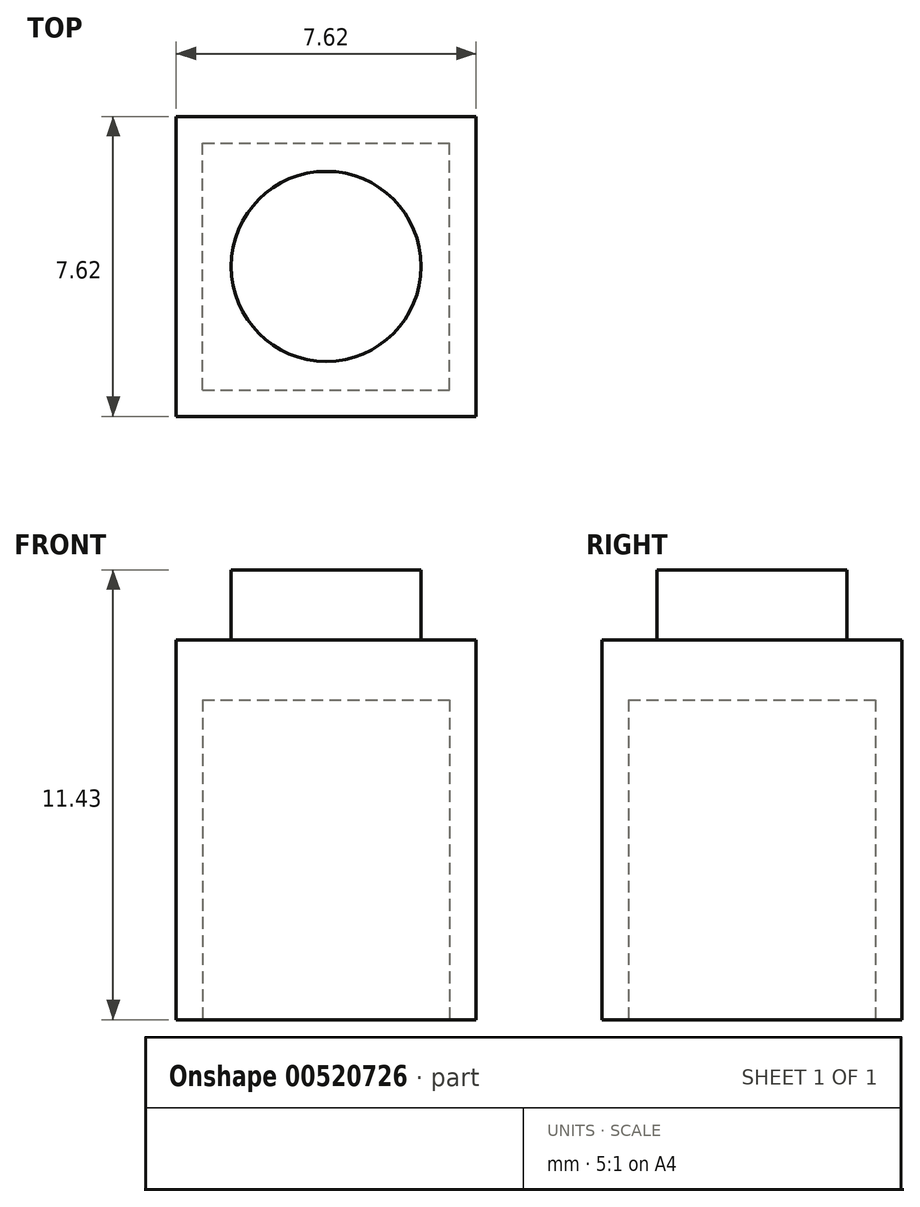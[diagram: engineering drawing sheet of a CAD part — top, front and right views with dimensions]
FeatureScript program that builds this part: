
annotation { "Feature Type Name" : "Feature", "Feature Type Description" : "" }
export const myFeature = defineFeature(function(context is Context, id is Id, definition is map)
    precondition{}
    {
        {
            var Q0;
            Q0=qCreatedBy(makeId("Top.planeOp"),FACE);
            var sketch = newSketch(context, id + "F0", { "sketchPlane" : qUnion([Q0])});
            skLineSegment(sketch, "E0.bottom", {"start": v(-3.8, 3.8) * mm, "end": v(3.81, 3.8) * mm});
            skLineSegment(sketch, "E0.top", {"start": v(-3.81, -3.81) * mm, "end": v(3.8, -3.81) * mm});
            skLineSegment(sketch, "E0.left", {"start": v(-3.8, 3.81) * mm, "end": v(-3.81, -3.81) * mm});
            skLineSegment(sketch, "E0.right", {"start": v(3.81, 3.8) * mm, "end": v(3.8, -3.81) * mm});
            skPoint(sketch, "E0.middle", {"position": v(0, 0) * mm});
            skSolve(sketch);
        }
        {
            var Q0;
            Q0=makeQuery(id+"F0.imprint","IMPRINT",FACE,{"disambiguationData":[TD([[makeQuery(id+"F0.imprint","IMPRINT",EDGE,{"derivedFrom":sQuery(id+"F0.wireOp",EDGE,"E0.bottom")}),-1.0]])]});
            extrude(context, id + "F1", {"entities" : qUnion([Q0]), "depth" : 9.65 * mm, "offsetDistance" : 25.4 * mm});
        }
        {
            var Q0;
            Q0=makeQuery(id+"F1.opExtrude","CAP_FACE",FACE,{"disambiguationData":[OSD([sQuery(id+"F0.wireOp",EDGE,"E0.bottom"),sQuery(id+"F0.wireOp",EDGE,"E0.top"),sQuery(id+"F0.wireOp",EDGE,"E0.left"),sQuery(id+"F0.wireOp",EDGE,"E0.right")])],"isStart":false});
            var sketch = newSketch(context, id + "F2", { "sketchPlane" : qUnion([Q0])});
            skCircle(sketch, "E1", {"center": v(0, 0) * mm, "radius": 2.41 * mm});
            skSolve(sketch);
        }
        {
            var Q0;
            Q0=makeQuery(id+"F2.imprint","IMPRINT",FACE,{"disambiguationData":[TD([[makeQuery(id+"F2.imprint","IMPRINT",EDGE,{"derivedFrom":sQuery(id+"F2.wireOp",EDGE,"E1")}),1.0]])]});
            extrude(context, id + "F3", {"entities" : qUnion([Q0]), "operationType" : NewBodyOperationType.ADD, "depth" : 1.78 * mm, "offsetDistance" : 25.4 * mm});
        }
        {
            var Q0;
            Q0=makeQuery(id+"F1.opExtrude","CAP_FACE",FACE,{"disambiguationData":[OSD([sQuery(id+"F0.wireOp",EDGE,"E0.bottom"),sQuery(id+"F0.wireOp",EDGE,"E0.top"),sQuery(id+"F0.wireOp",EDGE,"E0.left"),sQuery(id+"F0.wireOp",EDGE,"E0.right")])],"isStart":true});
            var sketch = newSketch(context, id + "F4", { "sketchPlane" : qUnion([Q0])});
            skLineSegment(sketch, "E2.bottom", {"start": v(-3.14, 3.14) * mm, "end": v(3.14, 3.14) * mm});
            skLineSegment(sketch, "E2.top", {"start": v(-3.14, -3.14) * mm, "end": v(3.14, -3.14) * mm});
            skLineSegment(sketch, "E2.left", {"start": v(-3.14, 3.14) * mm, "end": v(-3.14, -3.14) * mm});
            skLineSegment(sketch, "E2.right", {"start": v(3.14, 3.14) * mm, "end": v(3.14, -3.14) * mm});
            skPoint(sketch, "E2.middle", {"position": v(0, 0) * mm});
            skSolve(sketch);
        }
        {
            var Q0;
            Q0=makeQuery(id+"F4.imprint","IMPRINT",FACE,{"disambiguationData":[TD([[makeQuery(id+"F4.imprint","IMPRINT",EDGE,{"derivedFrom":sQuery(id+"F4.wireOp",EDGE,"E2.bottom")}),-1.0]])]});
            extrude(context, id + "F5", {"entities" : qUnion([Q0]), "operationType" : NewBodyOperationType.REMOVE, "oppositeDirection" : true, "depth" : 8.13 * mm, "offsetDistance" : 25.4 * mm});
        }
    });
